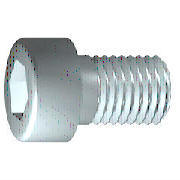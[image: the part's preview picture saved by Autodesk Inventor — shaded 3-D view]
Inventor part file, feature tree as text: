
AUTODESK INVENTOR PART (.ipt)
format: ipt  version: 2023 (Build 270158000, 158)  size: 186,368 bytes
history: native  units: mm (DEFAULTED — no unit token found)
features: sketch x2, other x1, extrude x1, plane x1, fillet x1
ambient origin geometry x7: Origin, YZ Plane, XY Plane, X Axis, Y Axis, Z Axis, Center Point
bodies: Solid1 (feature_tree)
feature tree (6):
  other  "Cuerpo"
  extrude  "Ranura"  Depth=2.0mm
  plane  "Work Plane1"
  fillet  "Fillet2"  Radius=2.0mm
  sketch  "Boceto1"  dims[d1=16.0mm d2=0.24548mm d3=2.0mm]
  sketch  "Boceto2"  dims[d4=1.0mm d5=60.0deg d6=2.0mm d7=2.0mm d8=1.732051mm d9=3.8mm d10=90.0deg d11=10.0mm d12=0.0mm d13=16.0mm d14=0.0mm d15=0.24538mm d16=0.24538mm d17=0.2mm d19=0.0mm d26=30.0mm d27=45.0deg d28=0.0mm d29=0.0mm d30=0.1mm]
